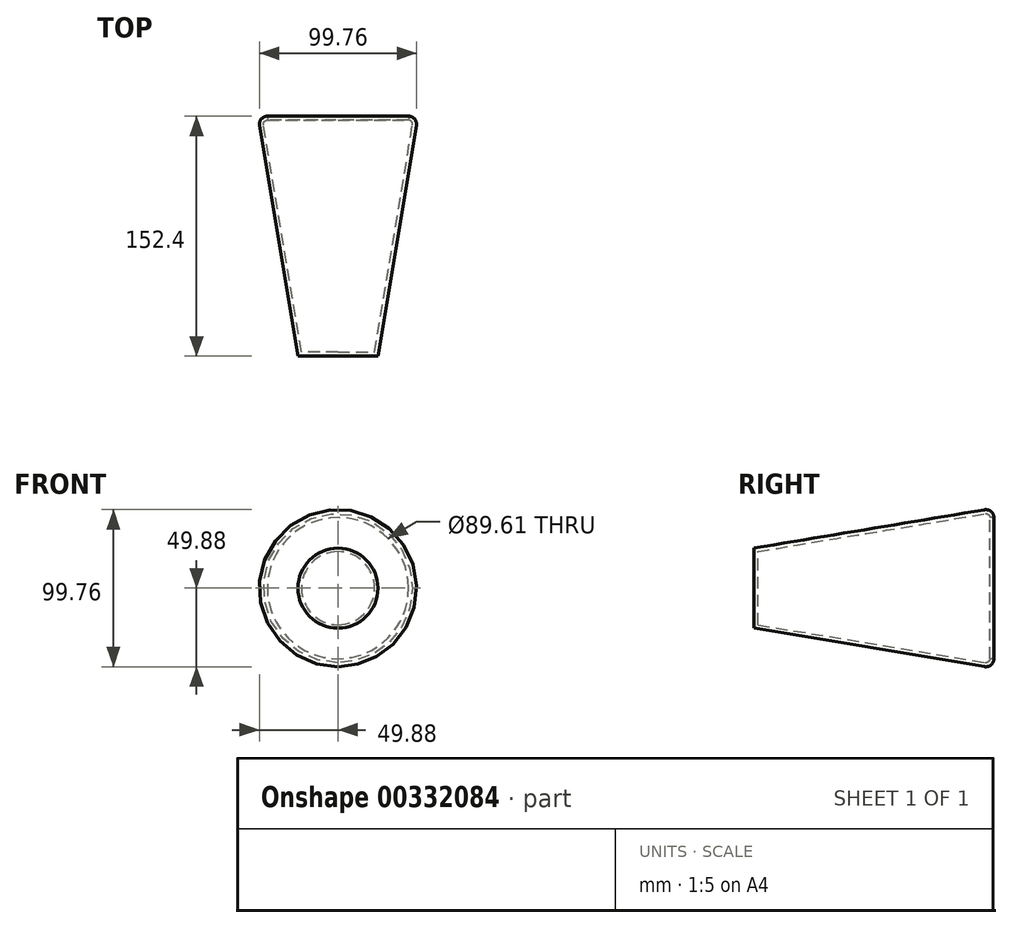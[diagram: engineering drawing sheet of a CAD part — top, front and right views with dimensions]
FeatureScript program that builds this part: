
annotation { "Feature Type Name" : "Feature", "Feature Type Description" : "" }
export const myFeature = defineFeature(function(context is Context, id is Id, definition is map)
    precondition{}
    {
        {
            var Q0;
            Q0=qCreatedBy(makeId("Front.planeOp"),FACE);
            cPlane(context, id + "F0", {"entities" : qUnion([Q0]), "cplaneType" : CPlaneType.OFFSET, "offset" : 76.2 * mm, "width" : 152.4 * mm, "height" : 152.4 * mm});
        }
        {
            var Q0;
            Q0=qCreatedBy(id+"F0.planeOp",FACE);
            cPlane(context, id + "F1", {"entities" : qUnion([Q0]), "cplaneType" : CPlaneType.OFFSET, "offset" : 76.2 * mm, "width" : 152.4 * mm, "height" : 152.4 * mm});
        }
        {
            var Q0;
            Q0=qCreatedBy(makeId("Front.planeOp"),FACE);
            var sketch = newSketch(context, id + "F2", { "sketchPlane" : qUnion([Q0])});
            skCircle(sketch, "E0", {"center": v(0, 0) * mm, "radius": 50.8 * mm});
            skSolve(sketch);
        }
        {
            var Q0;
            Q0=qCreatedBy(id+"F0.planeOp",FACE);
            var sketch = newSketch(context, id + "F3", { "sketchPlane" : qUnion([Q0])});
            skCircle(sketch, "E1", {"center": v(0, 0) * mm, "radius": 38.1 * mm});
            skSolve(sketch);
        }
        {
            var Q0;
            Q0=qCreatedBy(id+"F1.planeOp",FACE);
            var sketch = newSketch(context, id + "F4", { "sketchPlane" : qUnion([Q0])});
            skCircle(sketch, "E2", {"center": v(0, 0) * mm, "radius": 25.4 * mm});
            skSolve(sketch);
        }
        {
            var Q0;
            Q0=makeQuery(id+"F2.imprint","IMPRINT",FACE,{"disambiguationData":[TD([[makeQuery(id+"F2.imprint","IMPRINT",EDGE,{"derivedFrom":sQuery(id+"F2.wireOp",EDGE,"E0")}),1.0]])]});
            var Q1;
            Q1=makeQuery(id+"F3.imprint","IMPRINT",FACE,{"disambiguationData":[TD([[makeQuery(id+"F3.imprint","IMPRINT",EDGE,{"derivedFrom":sQuery(id+"F3.wireOp",EDGE,"E1")}),1.0]])]});
            var Q2;
            Q2=makeQuery(id+"F4.imprint","IMPRINT",FACE,{"disambiguationData":[TD([[makeQuery(id+"F4.imprint","IMPRINT",EDGE,{"derivedFrom":sQuery(id+"F4.wireOp",EDGE,"E2")}),1.0]])]});
            loft(context, id + "F5", {"sheetProfilesArray" : [{ "sheetProfileEntities" : qUnion([Q0]) }, { "sheetProfileEntities" : qUnion([Q1]) }, { "sheetProfileEntities" : qUnion([Q2]) }]});
        }
        {
            var Q0;
            Q0=makeQuery(id+"F5.opLoft","MID_CAP_EDGE",EDGE,{"disambiguationData":[OSD([sQuery(id+"F2.wireOp",EDGE,"E0")])],"capPos":0.0});
            fillet(context, id + "F6", {"entities" : qUnion([Q0]), "radius" : 5.08 * mm, "tangentPropagation" : true, "allowEdgeOverflow" : false});
        }
        {
            var Q0;
            Q0=makeQuery(id+"F5.opLoft","CAP_FACE",FACE,{"disambiguationData":[OSD([makeQuery(id+"F2.imprint","IMPRINT",FACE,{"disambiguationData":[TD([[makeQuery(id+"F2.imprint","IMPRINT",EDGE,{"derivedFrom":sQuery(id+"F2.wireOp",EDGE,"E0")}),1.0]])]})])],"isStart":true});
            shell(context, id + "F7", {"entities" : qUnion([Q0]), "thickness" : 2.54 * mm});
        }
    });
